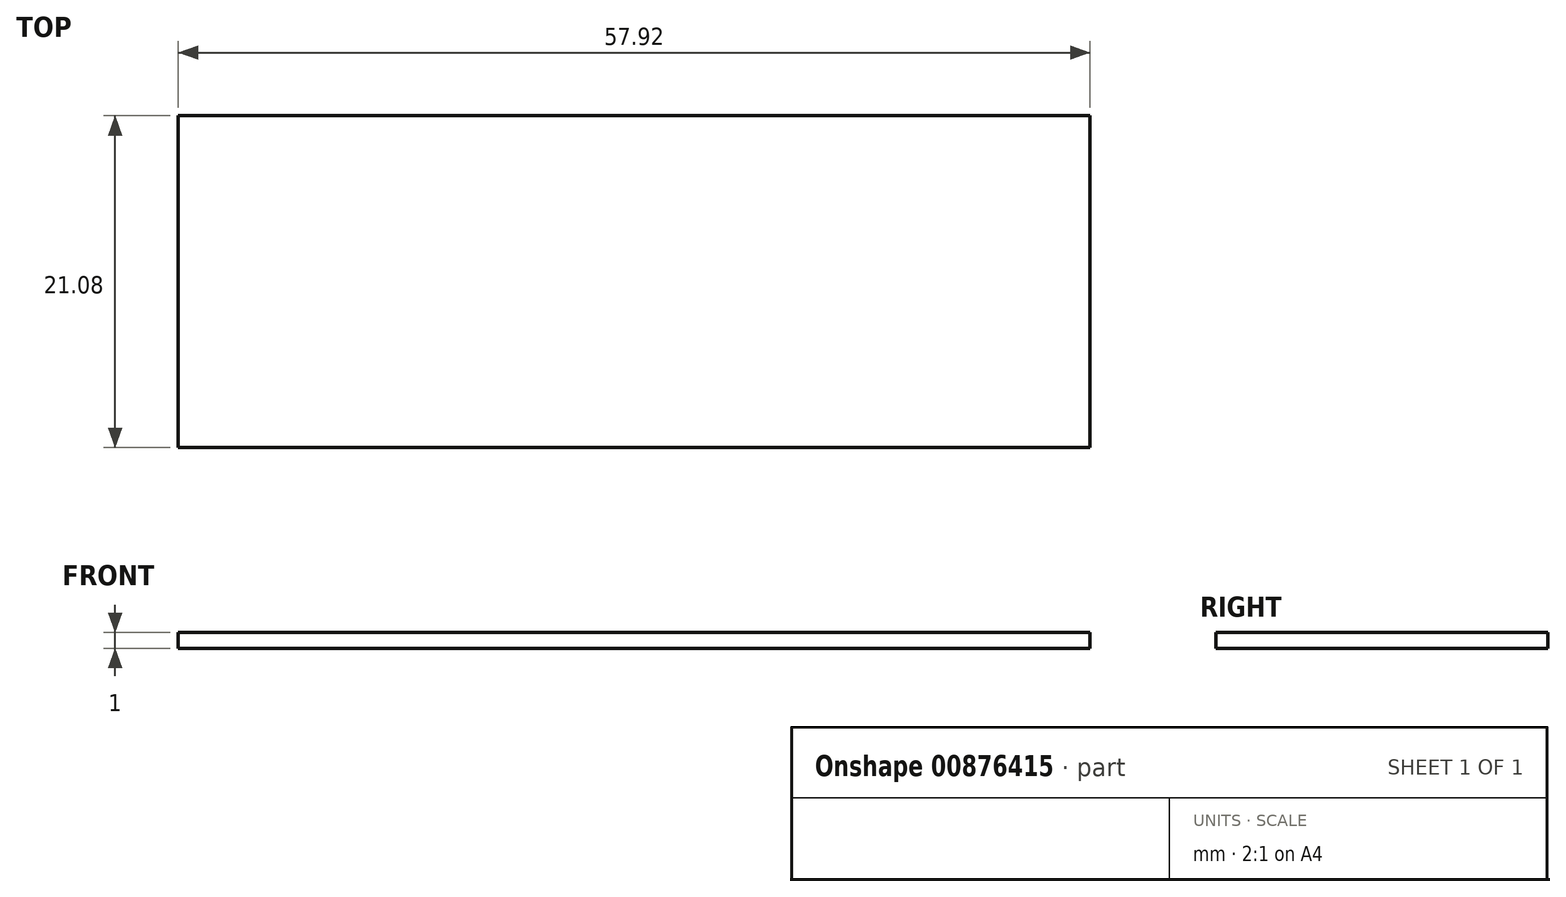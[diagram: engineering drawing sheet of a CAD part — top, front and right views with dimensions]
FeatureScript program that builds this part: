
annotation { "Feature Type Name" : "Feature", "Feature Type Description" : "" }
export const myFeature = defineFeature(function(context is Context, id is Id, definition is map)
    precondition{}
    {
        {
            var Q0;
            Q0=qCreatedBy(makeId("Top.planeOp"),FACE);
            var sketch = newSketch(context, id + "F0", { "sketchPlane" : qUnion([Q0])});
            skLineSegment(sketch, "E0.bottom", {"start": v(28.95, -10.54) * mm, "end": v(-28.95, -10.54) * mm});
            skLineSegment(sketch, "E0.top", {"start": v(28.95, 10.54) * mm, "end": v(-28.95, 10.54) * mm});
            skLineSegment(sketch, "E0.left", {"start": v(28.95, -10.54) * mm, "end": v(28.95, 10.54) * mm});
            skLineSegment(sketch, "E0.right", {"start": v(-28.95, -10.54) * mm, "end": v(-28.95, 10.54) * mm});
            skPoint(sketch, "E0.middle", {"position": v(0, 0) * mm});
            skSolve(sketch);
        }
        {
            var Q0;
            Q0=makeQuery(id+"F0.imprint","IMPRINT",FACE,{"disambiguationData":[TD([[makeQuery(id+"F0.imprint","IMPRINT",EDGE,{"derivedFrom":sQuery(id+"F0.wireOp",EDGE,"E0.bottom")}),-1.0]])]});
            extrude(context, id + "F1", {"entities" : qUnion([Q0]), "depth" : 1 * mm, "offsetDistance" : 25 * mm});
        }
    });
